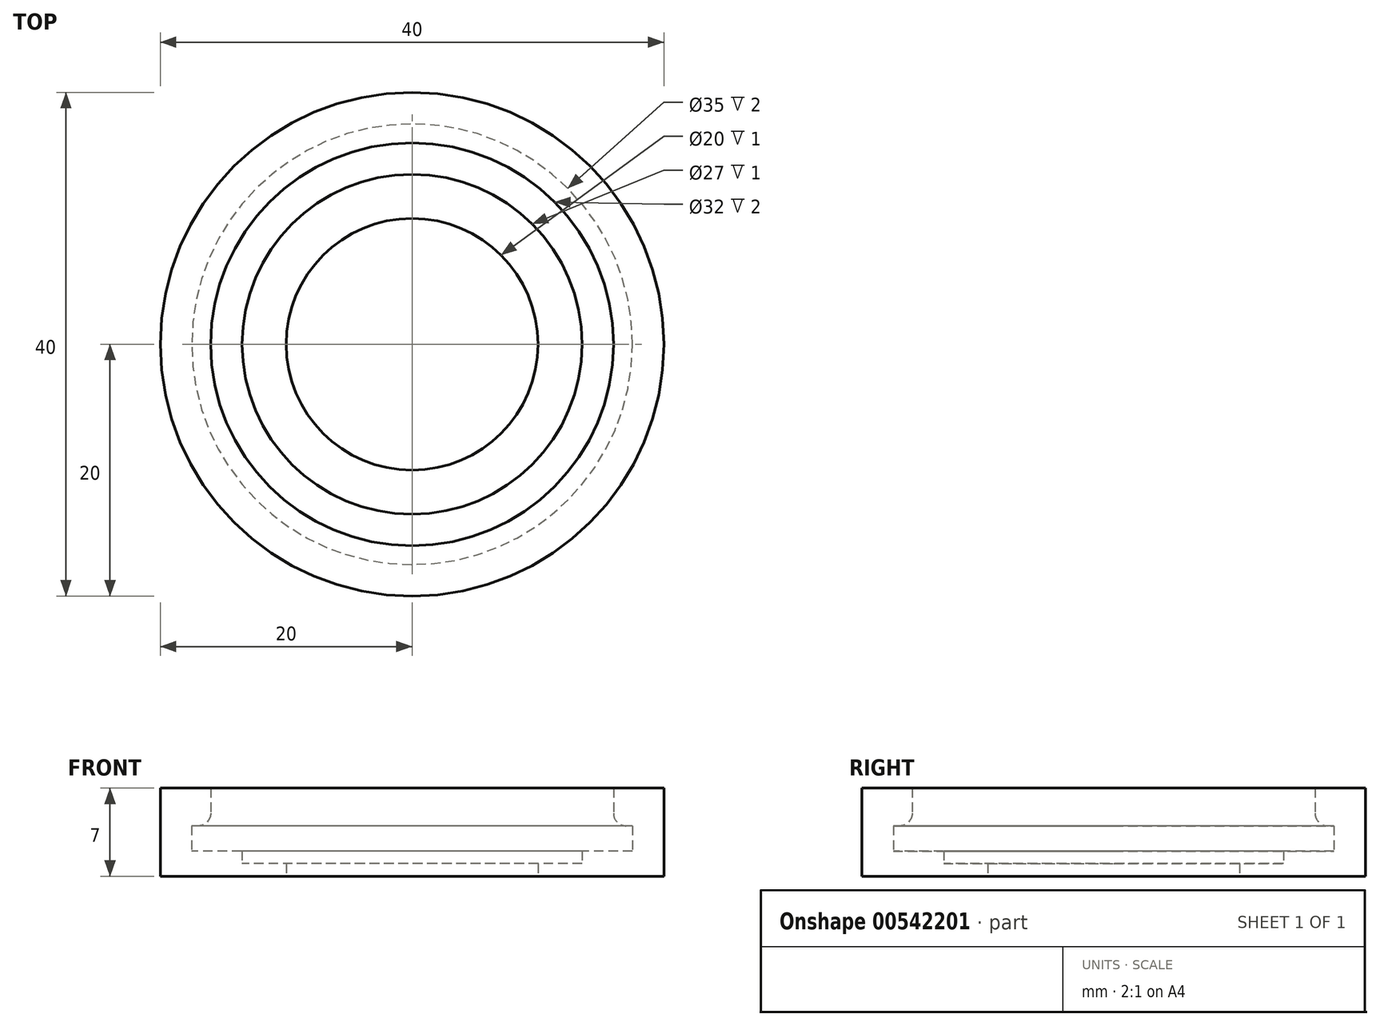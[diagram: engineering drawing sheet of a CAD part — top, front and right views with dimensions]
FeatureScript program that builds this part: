
annotation { "Feature Type Name" : "Feature", "Feature Type Description" : "" }
export const myFeature = defineFeature(function(context is Context, id is Id, definition is map)
    precondition{}
    {
        {
            var Q0;
            Q0=qCreatedBy(makeId("Top.planeOp"),FACE);
            var sketch = newSketch(context, id + "F0", { "sketchPlane" : qUnion([Q0])});
            skCircle(sketch, "E0", {"center": v(0, 0) * mm, "radius": 20 * mm});
            skCircle(sketch, "E1", {"center": v(0, 0) * mm, "radius": 10 * mm});
            skCircle(sketch, "E2", {"center": v(0, 0) * mm, "radius": 13.5 * mm});
            skCircle(sketch, "E3", {"center": v(0, 0) * mm, "radius": 17.5 * mm});
            skSolve(sketch);
        }
        {
            var Q0;
            Q0=makeQuery(id+"F0.imprint","IMPRINT",FACE,{"disambiguationData":[TD([[makeQuery(id+"F0.imprint","IMPRINT",EDGE,{"derivedFrom":sQuery(id+"F0.wireOp",EDGE,"E1")}),-1.0]])]});
            extrude(context, id + "F1", {"entities" : qUnion([Q0]), "depth" : 1 * mm, "offsetDistance" : 25 * mm});
        }
        {
            var Q0;
            Q0=makeQuery(id+"F0.imprint","IMPRINT",FACE,{"disambiguationData":[TD([[makeQuery(id+"F0.imprint","IMPRINT",EDGE,{"derivedFrom":sQuery(id+"F0.wireOp",EDGE,"E2")}),-1.0]])]});
            extrude(context, id + "F2", {"entities" : qUnion([Q0]), "operationType" : NewBodyOperationType.ADD, "depth" : 2 * mm, "offsetDistance" : 25 * mm});
        }
        {
            var Q0;
            Q0 = qSketchRegion(id + "F0", true);
            extrude(context, id + "F3", {"entities" : qUnion([Q0]), "operationType" : NewBodyOperationType.ADD, "depth" : 7 * mm, "offsetDistance" : 25 * mm});
        }
        {
            var Q0;
            Q0=qCreatedBy(makeId("Top.planeOp"),FACE);
            var sketch = newSketch(context, id + "F4", { "sketchPlane" : qUnion([Q0])});
            skCircle(sketch, "E4", {"center": v(0, 0) * mm, "radius": 20 * mm});
            skCircle(sketch, "E5", {"center": v(0, 0) * mm, "radius": 16 * mm});
            skSolve(sketch);
        }
        {
            var Q0;
            Q0 = qSketchRegion(id + "F4", true);
            extrude(context, id + "F5", {"entities" : qUnion([Q0]), "operationType" : NewBodyOperationType.ADD, "depth" : 7 * mm, "offsetDistance" : 25 * mm, "hasSecondDirection" : true, "secondDirectionOppositeDirection" : false, "secondDirectionDepth" : 4 * mm});
        }
        {
            var Q0;
            Q0=makeQuery(id+"F5.opExtrude","CAP_EDGE",EDGE,{"disambiguationData":[OSD([sQuery(id+"F4.wireOp",EDGE,"E5")])],"isStart":true});
            fillet(context, id + "F6", {"entities" : qUnion([Q0]), "radius" : 1 * mm, "tangentPropagation" : true, "allowEdgeOverflow" : false});
        }
    });
